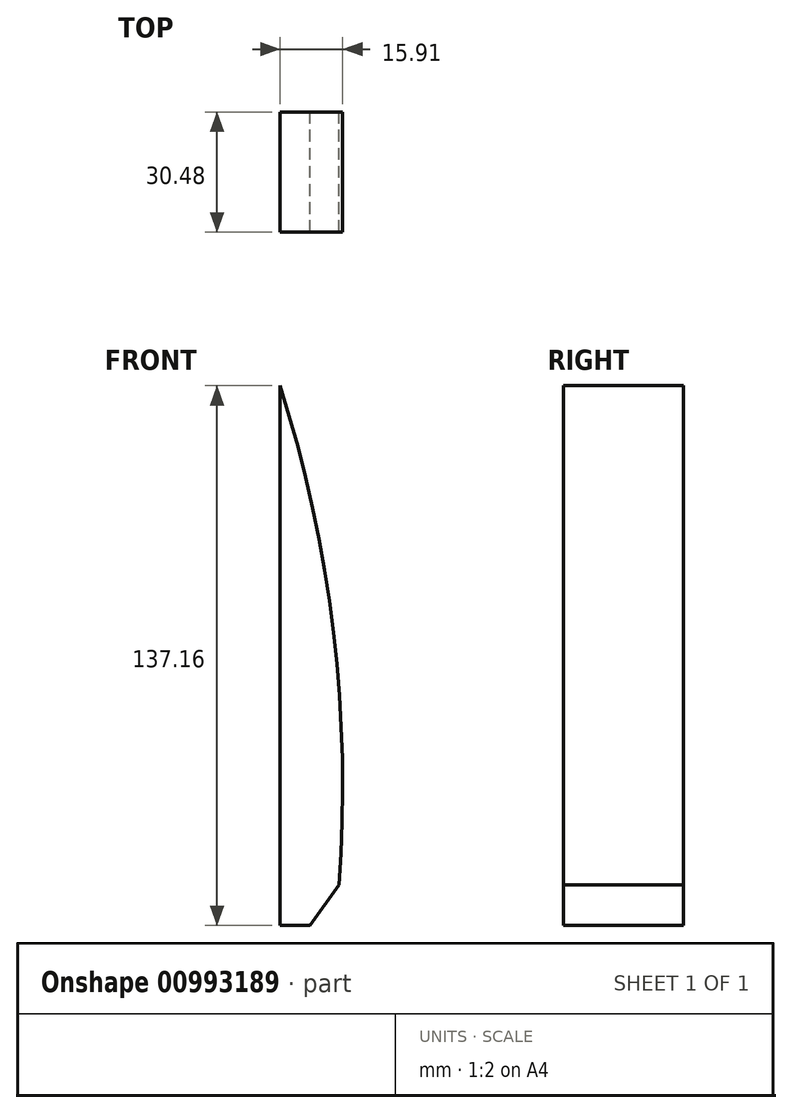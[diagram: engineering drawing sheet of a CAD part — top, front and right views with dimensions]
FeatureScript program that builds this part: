
annotation { "Feature Type Name" : "Feature", "Feature Type Description" : "" }
export const myFeature = defineFeature(function(context is Context, id is Id, definition is map)
    precondition{}
    {
        {
            var Q0;
            Q0=qCreatedBy(makeId("Right.planeOp"),FACE);
            var sketch = newSketch(context, id + "F0", { "sketchPlane" : qUnion([Q0])});
            skLineSegment(sketch, "E0.bottom", {"start": v(-52.06, 64.65) * mm, "end": v(-21.58, 64.65) * mm});
            skLineSegment(sketch, "E0.top", {"start": v(-52.06, -72.51) * mm, "end": v(-21.58, -72.51) * mm});
            skLineSegment(sketch, "E0.left", {"start": v(-52.06, 64.65) * mm, "end": v(-52.06, -72.51) * mm});
            skLineSegment(sketch, "E0.right", {"start": v(-21.58, 64.65) * mm, "end": v(-21.58, -72.51) * mm});
            skSolve(sketch);
        }
        {
            var Q0;
            Q0=makeQuery(id+"F0.imprint","IMPRINT",FACE,{"disambiguationData":[TD([[makeQuery(id+"F0.imprint","IMPRINT",EDGE,{"derivedFrom":sQuery(id+"F0.wireOp",EDGE,"E0.bottom")}),-1.0]])]});
            extrude(context, id + "F1", {"entities" : qUnion([Q0]), "depth" : 25.4 * mm, "offsetDistance" : 25.4 * mm});
        }
        {
            var Q0;
            Q0=makeQuery(id+"F1.opExtrude","SWEPT_FACE",FACE,{"disambiguationData":[OSD([sQuery(id+"F0.wireOp",EDGE,"E0.right")])]});
            var sketch = newSketch(context, id + "F2", { "sketchPlane" : qUnion([Q0])});
            skLineSegment(sketch, "E1", {"start": v(-7.62, -72.51) * mm, "end": v(-39.04, -28.69) * mm});
            skArc(sketch, "E2", {"start": v(0, 64.65) * mm, "mid": v(-13.6, 1.92) * mm, "end": v(-14.98, -62.25) * mm});
            skSolve(sketch);
        }
        {
            var Q0;
            {var subQ0=sQuery(id+"F2.wireOp",EDGE,"E1");var subQ4=makeQuery(id+"F2.imprint","INTERSECT",VERTEX,{"derivedFrom":[subQ0,sQuery(id+"F2.wireOp",EDGE,"E2")]});Q0=makeQuery(id+"F2.imprint","IMPRINT",FACE,{"disambiguationData":[TD([[makeQuery(id+"F2.imprint","IMPRINT",EDGE,{"disambiguationData":[TD([[subQ4,-1.0]])],"derivedFrom":subQ0}),1.0]])]});}
            var Q1;
            {var subQ0=sQuery(id+"F2.wireOp",EDGE,"E2");Q1=makeQuery(id+"F2.imprint","IMPRINT",FACE,{"disambiguationData":[TD([[makeQuery(id+"F2.imprint","IMPRINT",EDGE,{"derivedFrom":subQ0}),-1.0]])]});}
            extrude(context, id + "F3", {"entities" : qUnion([Q0, Q1]), "operationType" : NewBodyOperationType.REMOVE, "oppositeDirection" : true, "depth" : 50.8 * mm, "offsetDistance" : 25.4 * mm});
        }
    });
